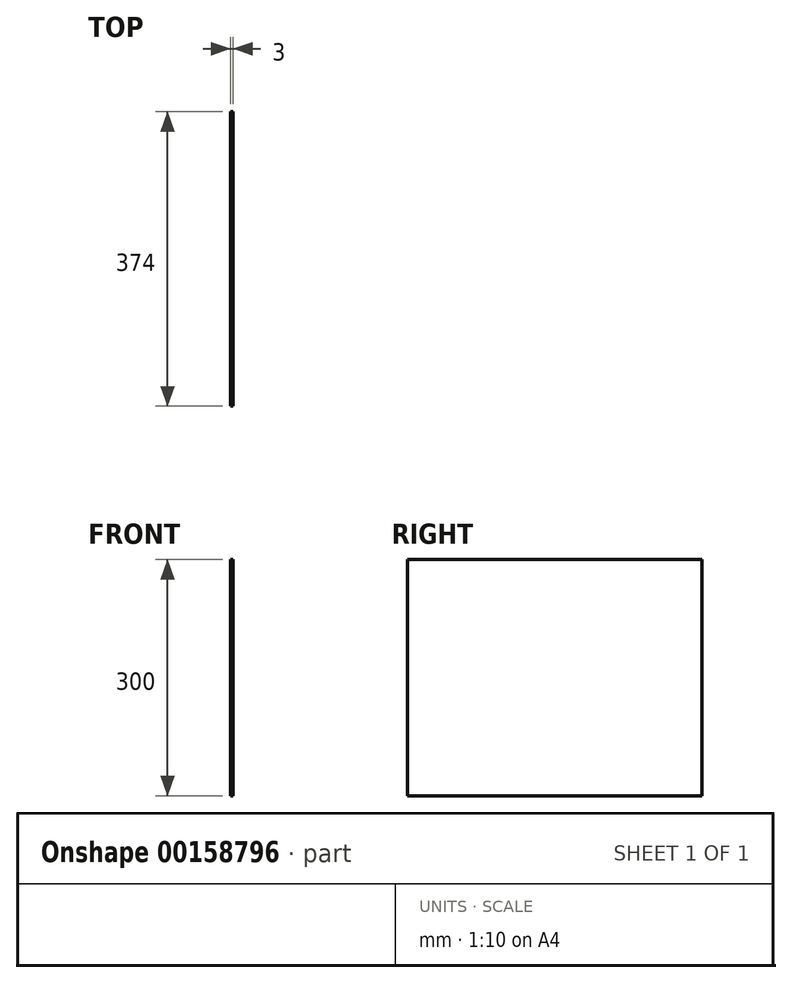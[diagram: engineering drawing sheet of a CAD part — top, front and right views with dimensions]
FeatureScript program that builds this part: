
annotation { "Feature Type Name" : "Feature", "Feature Type Description" : "" }
export const myFeature = defineFeature(function(context is Context, id is Id, definition is map)
    precondition{}
    {
        {
            var Q0;
            Q0=qCreatedBy(makeId("Top.planeOp"),FACE);
            var sketch = newSketch(context, id + "F0", { "sketchPlane" : qUnion([Q0])});
            skLineSegment(sketch, "E0.bottom", {"start": v(1.5, 187) * mm, "end": v(-1.5, 187) * mm});
            skLineSegment(sketch, "E0.top", {"start": v(1.5, -187) * mm, "end": v(-1.5, -187) * mm});
            skLineSegment(sketch, "E0.left", {"start": v(1.5, 187) * mm, "end": v(1.5, -187) * mm});
            skLineSegment(sketch, "E0.right", {"start": v(-1.5, 187) * mm, "end": v(-1.5, -187) * mm});
            skPoint(sketch, "E0.middle", {"position": v(0, 0) * mm});
            skSolve(sketch);
        }
        {
            var Q0;
            Q0 = qSketchRegion(id + "F0", true);
            extrude(context, id + "F1", {"entities" : qUnion([Q0]), "depth" : 300 * mm});
        }
    });
